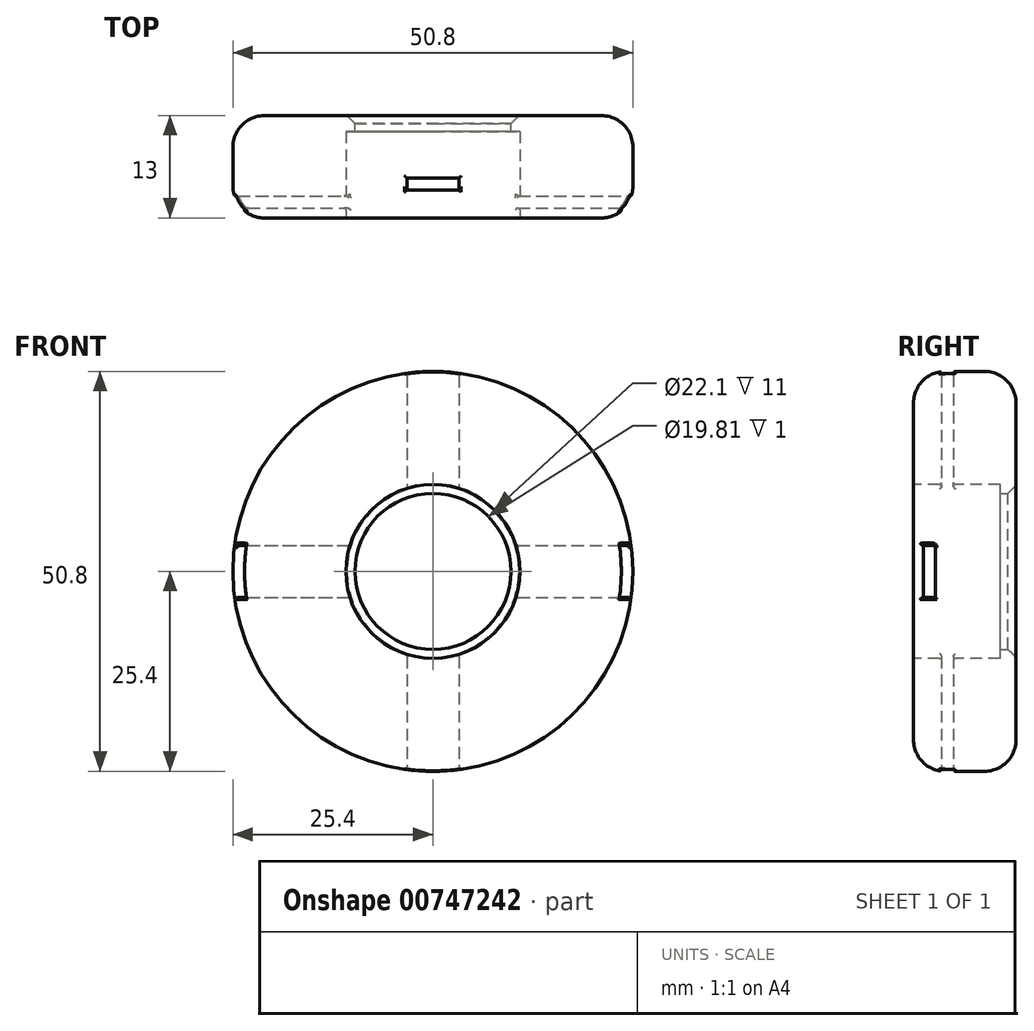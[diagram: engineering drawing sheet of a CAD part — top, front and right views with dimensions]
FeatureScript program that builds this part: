
annotation { "Feature Type Name" : "Feature", "Feature Type Description" : "" }
export const myFeature = defineFeature(function(context is Context, id is Id, definition is map)
    precondition{}
    {
        {
            var Q0;
            Q0=qCreatedBy(makeId("Front.planeOp"),FACE);
            var sketch = newSketch(context, id + "F0", { "sketchPlane" : qUnion([Q0])});
            skCircle(sketch, "E0", {"center": v(0, 0) * mm, "radius": 25.4 * mm});
            skSolve(sketch);
        }
        {
            var Q0;
            Q0=makeQuery(id+"F0.imprint","IMPRINT",FACE,{"disambiguationData":[TD([[makeQuery(id+"F0.imprint","IMPRINT",EDGE,{"derivedFrom":sQuery(id+"F0.wireOp",EDGE,"E0")}),1.0]])]});
            extrude(context, id + "F1", {"entities" : qUnion([Q0]), "depth" : 13 * mm, "offsetDistance" : 25.4 * mm});
        }
        {
            var Q0;
            Q0=qCreatedBy(makeId("Right.planeOp"),FACE);
            var sketch = newSketch(context, id + "F2", { "sketchPlane" : qUnion([Q0])});
            skLineSegment(sketch, "E1.bottom", {"start": v(-11.73, -3.3) * mm, "end": v(-10.2, -3.3) * mm});
            skLineSegment(sketch, "E1.top", {"start": v(-11.73, 3.3) * mm, "end": v(-10.2, 3.3) * mm});
            skLineSegment(sketch, "E1.left", {"start": v(-11.73, -3.3) * mm, "end": v(-11.73, 3.3) * mm});
            skLineSegment(sketch, "E1.right", {"start": v(-10.2, -3.3) * mm, "end": v(-10.2, 3.3) * mm});
            skSolve(sketch);
        }
        {
            var Q0;
            Q0 = qSketchRegion(id + "F2", true);
            extrude(context, id + "F3", {"entities" : qUnion([Q0]), "operationType" : NewBodyOperationType.REMOVE, "endBound" : BoundingType.THROUGH_ALL, "oppositeDirection" : true, "depth" : 25.4 * mm, "offsetDistance" : 25.4 * mm, "hasSecondDirection" : true, "secondDirectionOppositeDirection" : false, "secondDirectionDepth" : 25.4 * mm});
        }
        {
            var Q0;
            Q0=qCreatedBy(makeId("Top.planeOp"),FACE);
            var sketch = newSketch(context, id + "F4", { "sketchPlane" : qUnion([Q0])});
            skLineSegment(sketch, "E2.bottom", {"start": v(-3.3, -9.44) * mm, "end": v(3.3, -9.44) * mm});
            skLineSegment(sketch, "E2.top", {"start": v(-3.3, -7.92) * mm, "end": v(3.3, -7.92) * mm});
            skLineSegment(sketch, "E2.left", {"start": v(-3.3, -9.44) * mm, "end": v(-3.3, -7.92) * mm});
            skLineSegment(sketch, "E2.right", {"start": v(3.3, -9.44) * mm, "end": v(3.3, -7.92) * mm});
            skSolve(sketch);
        }
        {
            var Q0;
            Q0 = qSketchRegion(id + "F4", true);
            extrude(context, id + "F5", {"entities" : qUnion([Q0]), "operationType" : NewBodyOperationType.REMOVE, "endBound" : BoundingType.THROUGH_ALL, "depth" : 25.4 * mm, "offsetDistance" : 25.4 * mm, "hasSecondDirection" : true, "secondDirectionOppositeDirection" : true, "secondDirectionDepth" : 25.4 * mm});
        }
        {
            var Q0;
            Q0=makeQuery(id+"F1.opExtrude","CAP_FACE",FACE,{"disambiguationData":[OSD([sQuery(id+"F0.wireOp",EDGE,"E0")])],"isStart":false});
            var sketch = newSketch(context, id + "F6", { "sketchPlane" : qUnion([Q0])});
            skCircle(sketch, "E3", {"center": v(0, 0) * mm, "radius": 11.05 * mm});
            skSolve(sketch);
        }
        {
            var Q0;
            Q0=makeQuery(id+"F6.imprint","IMPRINT",FACE,{"disambiguationData":[TD([[makeQuery(id+"F6.imprint","IMPRINT",EDGE,{"derivedFrom":sQuery(id+"F6.wireOp",EDGE,"hlIgMGkD-AqOv-XqT3-OBZ0-IdH9VKwmBdzJ")}),1.0]])]});
            var Q1;
            Q1=makeQuery(id+"F6.imprint","IMPRINT",FACE,{"disambiguationData":[TD([[makeQuery(id+"F6.imprint","IMPRINT",EDGE,{"derivedFrom":sQuery(id+"F6.wireOp",EDGE,"E3")}),1.0]])]});
            extrude(context, id + "F7", {"entities" : qUnion([Q0, Q1]), "operationType" : NewBodyOperationType.REMOVE, "endBound" : BoundingType.THROUGH_ALL, "oppositeDirection" : true, "depth" : 25.4 * mm, "offsetDistance" : 25.4 * mm});
        }
        {
            var Q0;
            Q0=qCreatedBy(makeId("Front.planeOp"),FACE);
            var sketch = newSketch(context, id + "F8", { "sketchPlane" : qUnion([Q0])});
            skCircle(sketch, "E4", {"center": v(0, 0) * mm, "radius": 9.9 * mm});
            skCircle(sketch, "E5", {"center": v(0, 0) * mm, "radius": 11.05 * mm});
            skSolve(sketch);
        }
        {
            var Q0;
            Q0=makeQuery(id+"F8.imprint","IMPRINT",FACE,{"disambiguationData":[TD([[makeQuery(id+"F8.imprint","IMPRINT",EDGE,{"derivedFrom":sQuery(id+"F8.wireOp",EDGE,"E4")}),-1.0]])]});
            extrude(context, id + "F9", {"entities" : qUnion([Q0]), "operationType" : NewBodyOperationType.ADD, "depth" : 2 * mm, "offsetDistance" : 25.4 * mm});
        }
        {
            var Q0;
            Q0=makeQuery(id+"F1.opExtrude","CAP_EDGE",EDGE,{"disambiguationData":[OSD([sQuery(id+"F0.wireOp",EDGE,"E0")])],"isStart":false});
            var Q1;
            Q1=makeQuery(id+"F1.opExtrude","CAP_EDGE",EDGE,{"disambiguationData":[OSD([sQuery(id+"F0.wireOp",EDGE,"E0")])],"isStart":true});
            fillet(context, id + "F10", {"entities" : qUnion([Q0, Q1]), "radius" : 4 * mm, "tangentPropagation" : true, "allowEdgeOverflow" : false});
        }
        {
            var Q0;
            Q0=makeQuery(id+"F7.boolean.opBoolean","COPY",EDGE,{"derivedFrom":makeQuery(id+"F7.opExtrude","CAP_EDGE",EDGE,{"disambiguationData":[OSD([sQuery(id+"F6.wireOp",EDGE,"E3")])],"isStart":true})});
            var Q1;
            Q1=makeQuery(id+"F9.opExtrude","CAP_EDGE",EDGE,{"disambiguationData":[OSD([sQuery(id+"F8.wireOp",EDGE,"E4")])],"isStart":true});
            chamfer(context, id + "F11", {"entities" : qUnion([Q0, Q1]), "width" : 1 * mm, "tangentPropagation" : true});
        }
        {
            var Q0;
            Q0=makeQuery(id+"F7.boolean.opBoolean","INTERSECT",EDGE,{"disambiguationData":[OD(3.0)],"derivedFrom":[makeQuery(id+"F5.boolean.opBoolean","MERGE",FACE,{"derivedFrom":[makeQuery(id+"F3.boolean.opBoolean","COPY",FACE,{"derivedFrom":makeQuery(id+"F3.opExtrude","SWEPT_FACE",FACE,{"disambiguationData":[OSD([sQuery(id+"F2.wireOp",EDGE,"E1.right")])]})}),makeQuery(id+"F5.opExtrude","SWEPT_FACE",FACE,{"disambiguationData":[OSD([sQuery(id+"F4.wireOp",EDGE,"E2.top")])]})]}),makeQuery(id+"F7.opExtrude","SWEPT_FACE",FACE,{"disambiguationData":[OSD([sQuery(id+"F6.wireOp",EDGE,"E3")])]})]});
            var Q1;
            Q1=makeQuery(id+"F7.boolean.opBoolean","INTERSECT",EDGE,{"derivedFrom":[makeQuery(id+"F5.boolean.opBoolean","COPY",FACE,{"disambiguationData":[TD([makeQuery(id+"F3.boolean.opBoolean","COPY",FACE,{"derivedFrom":makeQuery(id+"F3.opExtrude","SWEPT_FACE",FACE,{"disambiguationData":[OSD([sQuery(id+"F2.wireOp",EDGE,"E1.top")])]})})])],"derivedFrom":makeQuery(id+"F5.opExtrude","SWEPT_FACE",FACE,{"disambiguationData":[OSD([sQuery(id+"F4.wireOp",EDGE,"E2.left")])]})}),makeQuery(id+"F7.opExtrude","SWEPT_FACE",FACE,{"disambiguationData":[OSD([sQuery(id+"F6.wireOp",EDGE,"E3")])]})]});
            var Q2;
            Q2=makeQuery(id+"F7.boolean.opBoolean","INTERSECT",EDGE,{"disambiguationData":[OD(3.0)],"derivedFrom":[makeQuery(id+"F5.boolean.opBoolean","MERGE",FACE,{"derivedFrom":[makeQuery(id+"F3.boolean.opBoolean","COPY",FACE,{"derivedFrom":makeQuery(id+"F3.opExtrude","SWEPT_FACE",FACE,{"disambiguationData":[OSD([sQuery(id+"F2.wireOp",EDGE,"E1.left")])]})}),makeQuery(id+"F5.opExtrude","SWEPT_FACE",FACE,{"disambiguationData":[OSD([sQuery(id+"F4.wireOp",EDGE,"E2.bottom")])]})]}),makeQuery(id+"F7.opExtrude","SWEPT_FACE",FACE,{"disambiguationData":[OSD([sQuery(id+"F6.wireOp",EDGE,"E3")])]})]});
            var Q3;
            Q3=makeQuery(id+"F7.boolean.opBoolean","INTERSECT",EDGE,{"derivedFrom":[makeQuery(id+"F5.boolean.opBoolean","COPY",FACE,{"disambiguationData":[TD([makeQuery(id+"F3.boolean.opBoolean","COPY",FACE,{"derivedFrom":makeQuery(id+"F3.opExtrude","SWEPT_FACE",FACE,{"disambiguationData":[OSD([sQuery(id+"F2.wireOp",EDGE,"E1.top")])]})})])],"derivedFrom":makeQuery(id+"F5.opExtrude","SWEPT_FACE",FACE,{"disambiguationData":[OSD([sQuery(id+"F4.wireOp",EDGE,"E2.right")])]})}),makeQuery(id+"F7.opExtrude","SWEPT_FACE",FACE,{"disambiguationData":[OSD([sQuery(id+"F6.wireOp",EDGE,"E3")])]})]});
            var Q4;
            Q4=makeQuery(id+"F7.boolean.opBoolean","INTERSECT",EDGE,{"derivedFrom":[makeQuery(id+"F5.boolean.opBoolean","SPLIT",FACE,{"disambiguationData":[TD([makeQuery(id+"F5.opExtrude","SWEPT_FACE",FACE,{"disambiguationData":[OSD([sQuery(id+"F4.wireOp",EDGE,"E2.left")])]})])],"derivedFrom":makeQuery(id+"F3.boolean.opBoolean","COPY",FACE,{"derivedFrom":makeQuery(id+"F3.opExtrude","SWEPT_FACE",FACE,{"disambiguationData":[OSD([sQuery(id+"F2.wireOp",EDGE,"E1.top")])]})})}),makeQuery(id+"F7.opExtrude","SWEPT_FACE",FACE,{"disambiguationData":[OSD([sQuery(id+"F6.wireOp",EDGE,"E3")])]})]});
            var Q5;
            Q5=makeQuery(id+"F7.boolean.opBoolean","INTERSECT",EDGE,{"disambiguationData":[OD(0.0)],"derivedFrom":[makeQuery(id+"F5.boolean.opBoolean","MERGE",FACE,{"derivedFrom":[makeQuery(id+"F3.boolean.opBoolean","COPY",FACE,{"derivedFrom":makeQuery(id+"F3.opExtrude","SWEPT_FACE",FACE,{"disambiguationData":[OSD([sQuery(id+"F2.wireOp",EDGE,"E1.right")])]})}),makeQuery(id+"F5.opExtrude","SWEPT_FACE",FACE,{"disambiguationData":[OSD([sQuery(id+"F4.wireOp",EDGE,"E2.top")])]})]}),makeQuery(id+"F7.opExtrude","SWEPT_FACE",FACE,{"disambiguationData":[OSD([sQuery(id+"F6.wireOp",EDGE,"E3")])]})]});
            var Q6;
            Q6=makeQuery(id+"F7.boolean.opBoolean","INTERSECT",EDGE,{"disambiguationData":[OD(0.0)],"derivedFrom":[makeQuery(id+"F5.boolean.opBoolean","MERGE",FACE,{"derivedFrom":[makeQuery(id+"F3.boolean.opBoolean","COPY",FACE,{"derivedFrom":makeQuery(id+"F3.opExtrude","SWEPT_FACE",FACE,{"disambiguationData":[OSD([sQuery(id+"F2.wireOp",EDGE,"E1.left")])]})}),makeQuery(id+"F5.opExtrude","SWEPT_FACE",FACE,{"disambiguationData":[OSD([sQuery(id+"F4.wireOp",EDGE,"E2.bottom")])]})]}),makeQuery(id+"F7.opExtrude","SWEPT_FACE",FACE,{"disambiguationData":[OSD([sQuery(id+"F6.wireOp",EDGE,"E3")])]})]});
            var Q7;
            Q7=makeQuery(id+"F7.boolean.opBoolean","INTERSECT",EDGE,{"derivedFrom":[makeQuery(id+"F5.boolean.opBoolean","SPLIT",FACE,{"disambiguationData":[TD([makeQuery(id+"F5.opExtrude","SWEPT_FACE",FACE,{"disambiguationData":[OSD([sQuery(id+"F4.wireOp",EDGE,"E2.left")])]})])],"derivedFrom":makeQuery(id+"F3.boolean.opBoolean","COPY",FACE,{"derivedFrom":makeQuery(id+"F3.opExtrude","SWEPT_FACE",FACE,{"disambiguationData":[OSD([sQuery(id+"F2.wireOp",EDGE,"E1.bottom")])]})})}),makeQuery(id+"F7.opExtrude","SWEPT_FACE",FACE,{"disambiguationData":[OSD([sQuery(id+"F6.wireOp",EDGE,"E3")])]})]});
            var Q8;
            Q8=makeQuery(id+"F7.boolean.opBoolean","INTERSECT",EDGE,{"derivedFrom":[makeQuery(id+"F5.boolean.opBoolean","COPY",FACE,{"disambiguationData":[TD([makeQuery(id+"F3.boolean.opBoolean","COPY",FACE,{"derivedFrom":makeQuery(id+"F3.opExtrude","SWEPT_FACE",FACE,{"disambiguationData":[OSD([sQuery(id+"F2.wireOp",EDGE,"E1.bottom")])]})})])],"derivedFrom":makeQuery(id+"F5.opExtrude","SWEPT_FACE",FACE,{"disambiguationData":[OSD([sQuery(id+"F4.wireOp",EDGE,"E2.right")])]})}),makeQuery(id+"F7.opExtrude","SWEPT_FACE",FACE,{"disambiguationData":[OSD([sQuery(id+"F6.wireOp",EDGE,"E3")])]})]});
            var Q9;
            Q9=makeQuery(id+"F7.boolean.opBoolean","INTERSECT",EDGE,{"disambiguationData":[OD(2.0)],"derivedFrom":[makeQuery(id+"F5.boolean.opBoolean","MERGE",FACE,{"derivedFrom":[makeQuery(id+"F3.boolean.opBoolean","COPY",FACE,{"derivedFrom":makeQuery(id+"F3.opExtrude","SWEPT_FACE",FACE,{"disambiguationData":[OSD([sQuery(id+"F2.wireOp",EDGE,"E1.right")])]})}),makeQuery(id+"F5.opExtrude","SWEPT_FACE",FACE,{"disambiguationData":[OSD([sQuery(id+"F4.wireOp",EDGE,"E2.top")])]})]}),makeQuery(id+"F7.opExtrude","SWEPT_FACE",FACE,{"disambiguationData":[OSD([sQuery(id+"F6.wireOp",EDGE,"E3")])]})]});
            var Q10;
            Q10=makeQuery(id+"F7.boolean.opBoolean","INTERSECT",EDGE,{"derivedFrom":[makeQuery(id+"F5.boolean.opBoolean","COPY",FACE,{"disambiguationData":[TD([makeQuery(id+"F3.boolean.opBoolean","COPY",FACE,{"derivedFrom":makeQuery(id+"F3.opExtrude","SWEPT_FACE",FACE,{"disambiguationData":[OSD([sQuery(id+"F2.wireOp",EDGE,"E1.bottom")])]})})])],"derivedFrom":makeQuery(id+"F5.opExtrude","SWEPT_FACE",FACE,{"disambiguationData":[OSD([sQuery(id+"F4.wireOp",EDGE,"E2.left")])]})}),makeQuery(id+"F7.opExtrude","SWEPT_FACE",FACE,{"disambiguationData":[OSD([sQuery(id+"F6.wireOp",EDGE,"E3")])]})]});
            var Q11;
            Q11=makeQuery(id+"F7.boolean.opBoolean","INTERSECT",EDGE,{"disambiguationData":[OD(2.0)],"derivedFrom":[makeQuery(id+"F5.boolean.opBoolean","MERGE",FACE,{"derivedFrom":[makeQuery(id+"F3.boolean.opBoolean","COPY",FACE,{"derivedFrom":makeQuery(id+"F3.opExtrude","SWEPT_FACE",FACE,{"disambiguationData":[OSD([sQuery(id+"F2.wireOp",EDGE,"E1.left")])]})}),makeQuery(id+"F5.opExtrude","SWEPT_FACE",FACE,{"disambiguationData":[OSD([sQuery(id+"F4.wireOp",EDGE,"E2.bottom")])]})]}),makeQuery(id+"F7.opExtrude","SWEPT_FACE",FACE,{"disambiguationData":[OSD([sQuery(id+"F6.wireOp",EDGE,"E3")])]})]});
            var Q12;
            Q12=makeQuery(id+"F7.boolean.opBoolean","INTERSECT",EDGE,{"disambiguationData":[OD(1.0)],"derivedFrom":[makeQuery(id+"F5.boolean.opBoolean","MERGE",FACE,{"derivedFrom":[makeQuery(id+"F3.boolean.opBoolean","COPY",FACE,{"derivedFrom":makeQuery(id+"F3.opExtrude","SWEPT_FACE",FACE,{"disambiguationData":[OSD([sQuery(id+"F2.wireOp",EDGE,"E1.left")])]})}),makeQuery(id+"F5.opExtrude","SWEPT_FACE",FACE,{"disambiguationData":[OSD([sQuery(id+"F4.wireOp",EDGE,"E2.bottom")])]})]}),makeQuery(id+"F7.opExtrude","SWEPT_FACE",FACE,{"disambiguationData":[OSD([sQuery(id+"F6.wireOp",EDGE,"E3")])]})]});
            var Q13;
            Q13=makeQuery(id+"F7.boolean.opBoolean","INTERSECT",EDGE,{"disambiguationData":[OD(1.0)],"derivedFrom":[makeQuery(id+"F5.boolean.opBoolean","MERGE",FACE,{"derivedFrom":[makeQuery(id+"F3.boolean.opBoolean","COPY",FACE,{"derivedFrom":makeQuery(id+"F3.opExtrude","SWEPT_FACE",FACE,{"disambiguationData":[OSD([sQuery(id+"F2.wireOp",EDGE,"E1.right")])]})}),makeQuery(id+"F5.opExtrude","SWEPT_FACE",FACE,{"disambiguationData":[OSD([sQuery(id+"F4.wireOp",EDGE,"E2.top")])]})]}),makeQuery(id+"F7.opExtrude","SWEPT_FACE",FACE,{"disambiguationData":[OSD([sQuery(id+"F6.wireOp",EDGE,"E3")])]})]});
            var Q14;
            Q14=makeQuery(id+"F7.boolean.opBoolean","INTERSECT",EDGE,{"derivedFrom":[makeQuery(id+"F5.boolean.opBoolean","SPLIT",FACE,{"disambiguationData":[TD([makeQuery(id+"F5.opExtrude","SWEPT_FACE",FACE,{"disambiguationData":[OSD([sQuery(id+"F4.wireOp",EDGE,"E2.right")])]})])],"derivedFrom":makeQuery(id+"F3.boolean.opBoolean","COPY",FACE,{"derivedFrom":makeQuery(id+"F3.opExtrude","SWEPT_FACE",FACE,{"disambiguationData":[OSD([sQuery(id+"F2.wireOp",EDGE,"E1.bottom")])]})})}),makeQuery(id+"F7.opExtrude","SWEPT_FACE",FACE,{"disambiguationData":[OSD([sQuery(id+"F6.wireOp",EDGE,"E3")])]})]});
            var Q15;
            Q15=makeQuery(id+"F7.boolean.opBoolean","INTERSECT",EDGE,{"derivedFrom":[makeQuery(id+"F5.boolean.opBoolean","SPLIT",FACE,{"disambiguationData":[TD([makeQuery(id+"F5.opExtrude","SWEPT_FACE",FACE,{"disambiguationData":[OSD([sQuery(id+"F4.wireOp",EDGE,"E2.right")])]})])],"derivedFrom":makeQuery(id+"F3.boolean.opBoolean","COPY",FACE,{"derivedFrom":makeQuery(id+"F3.opExtrude","SWEPT_FACE",FACE,{"disambiguationData":[OSD([sQuery(id+"F2.wireOp",EDGE,"E1.top")])]})})}),makeQuery(id+"F7.opExtrude","SWEPT_FACE",FACE,{"disambiguationData":[OSD([sQuery(id+"F6.wireOp",EDGE,"E3")])]})]});
            var Q16;
            {var subQ0=sQuery(id+"F0.wireOp",EDGE,"E0");var subQ1=makeQuery(id+"F1.opExtrude","SWEPT_FACE",FACE,{"disambiguationData":[OSD([subQ0])]});var subQ2=makeQuery(id+"F3.boolean.opBoolean","COPY",FACE,{"derivedFrom":makeQuery(id+"F3.opExtrude","SWEPT_FACE",FACE,{"disambiguationData":[OSD([sQuery(id+"F2.wireOp",EDGE,"E1.right")])]})});var subQ4=makeQuery(id+"F3.boolean.opBoolean","COPY",FACE,{"derivedFrom":makeQuery(id+"F3.opExtrude","SWEPT_FACE",FACE,{"disambiguationData":[OSD([sQuery(id+"F2.wireOp",EDGE,"E1.top")])]})});var subQ6=makeQuery(id+"F5.opExtrude","SWEPT_FACE",FACE,{"disambiguationData":[OSD([sQuery(id+"F4.wireOp",EDGE,"E2.top")])]});Q16=makeQuery(id+"F10.opFillet","BLEND_EDGE",EDGE,{"blendedFrom":[makeQuery(id+"F1.opExtrude","CAP_EDGE",EDGE,{"disambiguationData":[OSD([subQ0])],"isStart":false}),makeQuery(id+"F7.boolean.opBoolean","SPLIT",FACE,{"disambiguationData":[TD([subQ1,makeQuery(id+"F5.boolean.opBoolean","COPY",FACE,{"disambiguationData":[TD([subQ4])],"derivedFrom":makeQuery(id+"F5.opExtrude","SWEPT_FACE",FACE,{"disambiguationData":[OSD([sQuery(id+"F4.wireOp",EDGE,"E2.left")])]})}),makeQuery(id+"F5.boolean.opBoolean","COPY",FACE,{"disambiguationData":[TD([subQ4])],"derivedFrom":makeQuery(id+"F5.opExtrude","SWEPT_FACE",FACE,{"disambiguationData":[OSD([sQuery(id+"F4.wireOp",EDGE,"E2.right")])]})}),makeQuery(id+"F7.opExtrude","SWEPT_FACE",FACE,{"disambiguationData":[OSD([sQuery(id+"F6.wireOp",EDGE,"E3")])]})])],"derivedFrom":makeQuery(id+"F5.boolean.opBoolean","MERGE",FACE,{"derivedFrom":[subQ2,subQ6]})})],"blendedInto":[makeQuery(id+"F7.boolean.opBoolean","SPLIT",FACE,{"disambiguationData":[TD([subQ1,makeQuery(id+"F5.boolean.opBoolean","COPY",FACE,{"disambiguationData":[TD([subQ4])],"derivedFrom":makeQuery(id+"F5.opExtrude","SWEPT_FACE",FACE,{"disambiguationData":[OSD([sQuery(id+"F4.wireOp",EDGE,"E2.left")])]})}),makeQuery(id+"F5.boolean.opBoolean","COPY",FACE,{"disambiguationData":[TD([subQ4])],"derivedFrom":makeQuery(id+"F5.opExtrude","SWEPT_FACE",FACE,{"disambiguationData":[OSD([sQuery(id+"F4.wireOp",EDGE,"E2.right")])]})}),makeQuery(id+"F7.opExtrude","SWEPT_FACE",FACE,{"disambiguationData":[OSD([sQuery(id+"F6.wireOp",EDGE,"E3")])]})])],"derivedFrom":makeQuery(id+"F5.boolean.opBoolean","MERGE",FACE,{"derivedFrom":[subQ2,subQ6]})})]});}
            var Q17;
            {var subQ0=sQuery(id+"F0.wireOp",EDGE,"E0");Q17=makeQuery(id+"F10.opFillet","BLEND_EDGE",EDGE,{"blendedFrom":[makeQuery(id+"F1.opExtrude","CAP_EDGE",EDGE,{"disambiguationData":[OSD([subQ0])],"isStart":false}),makeQuery(id+"F5.boolean.opBoolean","COPY",FACE,{"disambiguationData":[TD([makeQuery(id+"F3.boolean.opBoolean","COPY",FACE,{"derivedFrom":makeQuery(id+"F3.opExtrude","SWEPT_FACE",FACE,{"disambiguationData":[OSD([sQuery(id+"F2.wireOp",EDGE,"E1.top")])]})})])],"derivedFrom":makeQuery(id+"F5.opExtrude","SWEPT_FACE",FACE,{"disambiguationData":[OSD([sQuery(id+"F4.wireOp",EDGE,"E2.right")])]})})],"blendedInto":[makeQuery(id+"F5.boolean.opBoolean","COPY",FACE,{"disambiguationData":[TD([makeQuery(id+"F3.boolean.opBoolean","COPY",FACE,{"derivedFrom":makeQuery(id+"F3.opExtrude","SWEPT_FACE",FACE,{"disambiguationData":[OSD([sQuery(id+"F2.wireOp",EDGE,"E1.top")])]})})])],"derivedFrom":makeQuery(id+"F5.opExtrude","SWEPT_FACE",FACE,{"disambiguationData":[OSD([sQuery(id+"F4.wireOp",EDGE,"E2.right")])]})})]});}
            var Q18;
            {var subQ0=sQuery(id+"F0.wireOp",EDGE,"E0");var subQ1=makeQuery(id+"F1.opExtrude","SWEPT_FACE",FACE,{"disambiguationData":[OSD([subQ0])]});var subQ3=makeQuery(id+"F3.boolean.opBoolean","COPY",FACE,{"derivedFrom":makeQuery(id+"F3.opExtrude","SWEPT_FACE",FACE,{"disambiguationData":[OSD([sQuery(id+"F2.wireOp",EDGE,"E1.left")])]})});var subQ4=makeQuery(id+"F3.boolean.opBoolean","COPY",FACE,{"derivedFrom":makeQuery(id+"F3.opExtrude","SWEPT_FACE",FACE,{"disambiguationData":[OSD([sQuery(id+"F2.wireOp",EDGE,"E1.top")])]})});var subQ5=makeQuery(id+"F5.opExtrude","SWEPT_FACE",FACE,{"disambiguationData":[OSD([sQuery(id+"F4.wireOp",EDGE,"E2.bottom")])]});Q18=makeQuery(id+"F10.opFillet","BLEND_EDGE",EDGE,{"blendedFrom":[makeQuery(id+"F1.opExtrude","CAP_EDGE",EDGE,{"disambiguationData":[OSD([subQ0])],"isStart":false}),makeQuery(id+"F7.boolean.opBoolean","SPLIT",FACE,{"disambiguationData":[TD([subQ1,makeQuery(id+"F5.boolean.opBoolean","COPY",FACE,{"disambiguationData":[TD([subQ4])],"derivedFrom":makeQuery(id+"F5.opExtrude","SWEPT_FACE",FACE,{"disambiguationData":[OSD([sQuery(id+"F4.wireOp",EDGE,"E2.left")])]})}),makeQuery(id+"F5.boolean.opBoolean","COPY",FACE,{"disambiguationData":[TD([subQ4])],"derivedFrom":makeQuery(id+"F5.opExtrude","SWEPT_FACE",FACE,{"disambiguationData":[OSD([sQuery(id+"F4.wireOp",EDGE,"E2.right")])]})}),makeQuery(id+"F7.opExtrude","SWEPT_FACE",FACE,{"disambiguationData":[OSD([sQuery(id+"F6.wireOp",EDGE,"E3")])]})])],"derivedFrom":makeQuery(id+"F5.boolean.opBoolean","MERGE",FACE,{"derivedFrom":[subQ3,subQ5]})})],"blendedInto":[makeQuery(id+"F7.boolean.opBoolean","SPLIT",FACE,{"disambiguationData":[TD([subQ1,makeQuery(id+"F5.boolean.opBoolean","COPY",FACE,{"disambiguationData":[TD([subQ4])],"derivedFrom":makeQuery(id+"F5.opExtrude","SWEPT_FACE",FACE,{"disambiguationData":[OSD([sQuery(id+"F4.wireOp",EDGE,"E2.left")])]})}),makeQuery(id+"F5.boolean.opBoolean","COPY",FACE,{"disambiguationData":[TD([subQ4])],"derivedFrom":makeQuery(id+"F5.opExtrude","SWEPT_FACE",FACE,{"disambiguationData":[OSD([sQuery(id+"F4.wireOp",EDGE,"E2.right")])]})}),makeQuery(id+"F7.opExtrude","SWEPT_FACE",FACE,{"disambiguationData":[OSD([sQuery(id+"F6.wireOp",EDGE,"E3")])]})])],"derivedFrom":makeQuery(id+"F5.boolean.opBoolean","MERGE",FACE,{"derivedFrom":[subQ3,subQ5]})})]});}
            var Q19;
            {var subQ0=sQuery(id+"F0.wireOp",EDGE,"E0");Q19=makeQuery(id+"F10.opFillet","BLEND_EDGE",EDGE,{"blendedFrom":[makeQuery(id+"F1.opExtrude","CAP_EDGE",EDGE,{"disambiguationData":[OSD([subQ0])],"isStart":false}),makeQuery(id+"F5.boolean.opBoolean","COPY",FACE,{"disambiguationData":[TD([makeQuery(id+"F3.boolean.opBoolean","COPY",FACE,{"derivedFrom":makeQuery(id+"F3.opExtrude","SWEPT_FACE",FACE,{"disambiguationData":[OSD([sQuery(id+"F2.wireOp",EDGE,"E1.top")])]})})])],"derivedFrom":makeQuery(id+"F5.opExtrude","SWEPT_FACE",FACE,{"disambiguationData":[OSD([sQuery(id+"F4.wireOp",EDGE,"E2.left")])]})})],"blendedInto":[makeQuery(id+"F5.boolean.opBoolean","COPY",FACE,{"disambiguationData":[TD([makeQuery(id+"F3.boolean.opBoolean","COPY",FACE,{"derivedFrom":makeQuery(id+"F3.opExtrude","SWEPT_FACE",FACE,{"disambiguationData":[OSD([sQuery(id+"F2.wireOp",EDGE,"E1.top")])]})})])],"derivedFrom":makeQuery(id+"F5.opExtrude","SWEPT_FACE",FACE,{"disambiguationData":[OSD([sQuery(id+"F4.wireOp",EDGE,"E2.left")])]})})]});}
            var Q20;
            {var subQ0=sQuery(id+"F0.wireOp",EDGE,"E0");Q20=makeQuery(id+"F10.opFillet","BLEND_EDGE",EDGE,{"blendedFrom":[makeQuery(id+"F1.opExtrude","CAP_EDGE",EDGE,{"disambiguationData":[OSD([subQ0])],"isStart":false}),makeQuery(id+"F5.boolean.opBoolean","SPLIT",FACE,{"disambiguationData":[TD([makeQuery(id+"F5.opExtrude","SWEPT_FACE",FACE,{"disambiguationData":[OSD([sQuery(id+"F4.wireOp",EDGE,"E2.left")])]})])],"derivedFrom":makeQuery(id+"F3.boolean.opBoolean","COPY",FACE,{"derivedFrom":makeQuery(id+"F3.opExtrude","SWEPT_FACE",FACE,{"disambiguationData":[OSD([sQuery(id+"F2.wireOp",EDGE,"E1.bottom")])]})})})],"blendedInto":[makeQuery(id+"F5.boolean.opBoolean","SPLIT",FACE,{"disambiguationData":[TD([makeQuery(id+"F5.opExtrude","SWEPT_FACE",FACE,{"disambiguationData":[OSD([sQuery(id+"F4.wireOp",EDGE,"E2.left")])]})])],"derivedFrom":makeQuery(id+"F3.boolean.opBoolean","COPY",FACE,{"derivedFrom":makeQuery(id+"F3.opExtrude","SWEPT_FACE",FACE,{"disambiguationData":[OSD([sQuery(id+"F2.wireOp",EDGE,"E1.bottom")])]})})})]});}
            var Q21;
            {var subQ0=sQuery(id+"F0.wireOp",EDGE,"E0");Q21=makeQuery(id+"F10.opFillet","BLEND_EDGE",EDGE,{"blendedFrom":[makeQuery(id+"F1.opExtrude","CAP_EDGE",EDGE,{"disambiguationData":[OSD([subQ0])],"isStart":false}),makeQuery(id+"F7.boolean.opBoolean","SPLIT",FACE,{"disambiguationData":[TD([makeQuery(id+"F1.opExtrude","SWEPT_FACE",FACE,{"disambiguationData":[OSD([subQ0])]}),makeQuery(id+"F3.boolean.opBoolean","COPY",FACE,{"derivedFrom":makeQuery(id+"F3.opExtrude","SWEPT_FACE",FACE,{"disambiguationData":[OSD([sQuery(id+"F2.wireOp",EDGE,"E1.bottom")])]})}),makeQuery(id+"F3.boolean.opBoolean","COPY",FACE,{"derivedFrom":makeQuery(id+"F3.opExtrude","SWEPT_FACE",FACE,{"disambiguationData":[OSD([sQuery(id+"F2.wireOp",EDGE,"E1.top")])]})}),makeQuery(id+"F7.opExtrude","SWEPT_FACE",FACE,{"disambiguationData":[OSD([sQuery(id+"F6.wireOp",EDGE,"E3")])]})]),OD(0.0)],"derivedFrom":makeQuery(id+"F5.boolean.opBoolean","MERGE",FACE,{"derivedFrom":[makeQuery(id+"F3.boolean.opBoolean","COPY",FACE,{"derivedFrom":makeQuery(id+"F3.opExtrude","SWEPT_FACE",FACE,{"disambiguationData":[OSD([sQuery(id+"F2.wireOp",EDGE,"E1.right")])]})}),makeQuery(id+"F5.opExtrude","SWEPT_FACE",FACE,{"disambiguationData":[OSD([sQuery(id+"F4.wireOp",EDGE,"E2.top")])]})]})})],"blendedInto":[makeQuery(id+"F7.boolean.opBoolean","SPLIT",FACE,{"disambiguationData":[TD([makeQuery(id+"F1.opExtrude","SWEPT_FACE",FACE,{"disambiguationData":[OSD([subQ0])]}),makeQuery(id+"F3.boolean.opBoolean","COPY",FACE,{"derivedFrom":makeQuery(id+"F3.opExtrude","SWEPT_FACE",FACE,{"disambiguationData":[OSD([sQuery(id+"F2.wireOp",EDGE,"E1.bottom")])]})}),makeQuery(id+"F3.boolean.opBoolean","COPY",FACE,{"derivedFrom":makeQuery(id+"F3.opExtrude","SWEPT_FACE",FACE,{"disambiguationData":[OSD([sQuery(id+"F2.wireOp",EDGE,"E1.top")])]})}),makeQuery(id+"F7.opExtrude","SWEPT_FACE",FACE,{"disambiguationData":[OSD([sQuery(id+"F6.wireOp",EDGE,"E3")])]})]),OD(0.0)],"derivedFrom":makeQuery(id+"F5.boolean.opBoolean","MERGE",FACE,{"derivedFrom":[makeQuery(id+"F3.boolean.opBoolean","COPY",FACE,{"derivedFrom":makeQuery(id+"F3.opExtrude","SWEPT_FACE",FACE,{"disambiguationData":[OSD([sQuery(id+"F2.wireOp",EDGE,"E1.right")])]})}),makeQuery(id+"F5.opExtrude","SWEPT_FACE",FACE,{"disambiguationData":[OSD([sQuery(id+"F4.wireOp",EDGE,"E2.top")])]})]})})]});}
            var Q22;
            {var subQ0=sQuery(id+"F0.wireOp",EDGE,"E0");Q22=makeQuery(id+"F10.opFillet","BLEND_EDGE",EDGE,{"blendedFrom":[makeQuery(id+"F1.opExtrude","CAP_EDGE",EDGE,{"disambiguationData":[OSD([subQ0])],"isStart":false}),makeQuery(id+"F7.boolean.opBoolean","SPLIT",FACE,{"disambiguationData":[TD([makeQuery(id+"F1.opExtrude","SWEPT_FACE",FACE,{"disambiguationData":[OSD([subQ0])]}),makeQuery(id+"F3.boolean.opBoolean","COPY",FACE,{"derivedFrom":makeQuery(id+"F3.opExtrude","SWEPT_FACE",FACE,{"disambiguationData":[OSD([sQuery(id+"F2.wireOp",EDGE,"E1.bottom")])]})}),makeQuery(id+"F3.boolean.opBoolean","COPY",FACE,{"derivedFrom":makeQuery(id+"F3.opExtrude","SWEPT_FACE",FACE,{"disambiguationData":[OSD([sQuery(id+"F2.wireOp",EDGE,"E1.top")])]})}),makeQuery(id+"F7.opExtrude","SWEPT_FACE",FACE,{"disambiguationData":[OSD([sQuery(id+"F6.wireOp",EDGE,"E3")])]})]),OD(0.0)],"derivedFrom":makeQuery(id+"F5.boolean.opBoolean","MERGE",FACE,{"derivedFrom":[makeQuery(id+"F3.boolean.opBoolean","COPY",FACE,{"derivedFrom":makeQuery(id+"F3.opExtrude","SWEPT_FACE",FACE,{"disambiguationData":[OSD([sQuery(id+"F2.wireOp",EDGE,"E1.left")])]})}),makeQuery(id+"F5.opExtrude","SWEPT_FACE",FACE,{"disambiguationData":[OSD([sQuery(id+"F4.wireOp",EDGE,"E2.bottom")])]})]})})],"blendedInto":[makeQuery(id+"F7.boolean.opBoolean","SPLIT",FACE,{"disambiguationData":[TD([makeQuery(id+"F1.opExtrude","SWEPT_FACE",FACE,{"disambiguationData":[OSD([subQ0])]}),makeQuery(id+"F3.boolean.opBoolean","COPY",FACE,{"derivedFrom":makeQuery(id+"F3.opExtrude","SWEPT_FACE",FACE,{"disambiguationData":[OSD([sQuery(id+"F2.wireOp",EDGE,"E1.bottom")])]})}),makeQuery(id+"F3.boolean.opBoolean","COPY",FACE,{"derivedFrom":makeQuery(id+"F3.opExtrude","SWEPT_FACE",FACE,{"disambiguationData":[OSD([sQuery(id+"F2.wireOp",EDGE,"E1.top")])]})}),makeQuery(id+"F7.opExtrude","SWEPT_FACE",FACE,{"disambiguationData":[OSD([sQuery(id+"F6.wireOp",EDGE,"E3")])]})]),OD(0.0)],"derivedFrom":makeQuery(id+"F5.boolean.opBoolean","MERGE",FACE,{"derivedFrom":[makeQuery(id+"F3.boolean.opBoolean","COPY",FACE,{"derivedFrom":makeQuery(id+"F3.opExtrude","SWEPT_FACE",FACE,{"disambiguationData":[OSD([sQuery(id+"F2.wireOp",EDGE,"E1.left")])]})}),makeQuery(id+"F5.opExtrude","SWEPT_FACE",FACE,{"disambiguationData":[OSD([sQuery(id+"F4.wireOp",EDGE,"E2.bottom")])]})]})})]});}
            var Q23;
            {var subQ0=sQuery(id+"F2.wireOp",EDGE,"E1.right");var subQ1=sQuery(id+"F2.wireOp",EDGE,"E1.top");Q23=makeQuery(id+"F5.boolean.opBoolean","SPLIT",EDGE,{"disambiguationData":[TD([makeQuery(id+"F5.opExtrude","SWEPT_FACE",FACE,{"disambiguationData":[OSD([sQuery(id+"F4.wireOp",EDGE,"E2.left")])]})])],"derivedFrom":makeQuery(id+"F3.boolean.opBoolean","COPY",EDGE,{"derivedFrom":makeQuery(id+"F3.opExtrude","SWEPT_EDGE",EDGE,{"disambiguationData":[OSD([subQ1,subQ0])]})})});}
            var Q24;
            {var subQ0=sQuery(id+"F0.wireOp",EDGE,"E0");Q24=makeQuery(id+"F10.opFillet","BLEND_EDGE",EDGE,{"blendedFrom":[makeQuery(id+"F1.opExtrude","CAP_EDGE",EDGE,{"disambiguationData":[OSD([subQ0])],"isStart":false}),makeQuery(id+"F5.boolean.opBoolean","COPY",FACE,{"disambiguationData":[TD([makeQuery(id+"F3.boolean.opBoolean","COPY",FACE,{"derivedFrom":makeQuery(id+"F3.opExtrude","SWEPT_FACE",FACE,{"disambiguationData":[OSD([sQuery(id+"F2.wireOp",EDGE,"E1.bottom")])]})})])],"derivedFrom":makeQuery(id+"F5.opExtrude","SWEPT_FACE",FACE,{"disambiguationData":[OSD([sQuery(id+"F4.wireOp",EDGE,"E2.right")])]})})],"blendedInto":[makeQuery(id+"F5.boolean.opBoolean","COPY",FACE,{"disambiguationData":[TD([makeQuery(id+"F3.boolean.opBoolean","COPY",FACE,{"derivedFrom":makeQuery(id+"F3.opExtrude","SWEPT_FACE",FACE,{"disambiguationData":[OSD([sQuery(id+"F2.wireOp",EDGE,"E1.bottom")])]})})])],"derivedFrom":makeQuery(id+"F5.opExtrude","SWEPT_FACE",FACE,{"disambiguationData":[OSD([sQuery(id+"F4.wireOp",EDGE,"E2.right")])]})})]});}
            var Q25;
            {var subQ0=sQuery(id+"F0.wireOp",EDGE,"E0");var subQ1=makeQuery(id+"F1.opExtrude","SWEPT_FACE",FACE,{"disambiguationData":[OSD([subQ0])]});var subQ3=makeQuery(id+"F3.boolean.opBoolean","COPY",FACE,{"derivedFrom":makeQuery(id+"F3.opExtrude","SWEPT_FACE",FACE,{"disambiguationData":[OSD([sQuery(id+"F2.wireOp",EDGE,"E1.left")])]})});var subQ4=makeQuery(id+"F3.boolean.opBoolean","COPY",FACE,{"derivedFrom":makeQuery(id+"F3.opExtrude","SWEPT_FACE",FACE,{"disambiguationData":[OSD([sQuery(id+"F2.wireOp",EDGE,"E1.bottom")])]})});var subQ5=makeQuery(id+"F5.opExtrude","SWEPT_FACE",FACE,{"disambiguationData":[OSD([sQuery(id+"F4.wireOp",EDGE,"E2.bottom")])]});Q25=makeQuery(id+"F10.opFillet","BLEND_EDGE",EDGE,{"blendedFrom":[makeQuery(id+"F1.opExtrude","CAP_EDGE",EDGE,{"disambiguationData":[OSD([subQ0])],"isStart":false}),makeQuery(id+"F7.boolean.opBoolean","SPLIT",FACE,{"disambiguationData":[TD([subQ1,makeQuery(id+"F5.boolean.opBoolean","COPY",FACE,{"disambiguationData":[TD([subQ4])],"derivedFrom":makeQuery(id+"F5.opExtrude","SWEPT_FACE",FACE,{"disambiguationData":[OSD([sQuery(id+"F4.wireOp",EDGE,"E2.left")])]})}),makeQuery(id+"F5.boolean.opBoolean","COPY",FACE,{"disambiguationData":[TD([subQ4])],"derivedFrom":makeQuery(id+"F5.opExtrude","SWEPT_FACE",FACE,{"disambiguationData":[OSD([sQuery(id+"F4.wireOp",EDGE,"E2.right")])]})}),makeQuery(id+"F7.opExtrude","SWEPT_FACE",FACE,{"disambiguationData":[OSD([sQuery(id+"F6.wireOp",EDGE,"E3")])]})])],"derivedFrom":makeQuery(id+"F5.boolean.opBoolean","MERGE",FACE,{"derivedFrom":[subQ3,subQ5]})})],"blendedInto":[makeQuery(id+"F7.boolean.opBoolean","SPLIT",FACE,{"disambiguationData":[TD([subQ1,makeQuery(id+"F5.boolean.opBoolean","COPY",FACE,{"disambiguationData":[TD([subQ4])],"derivedFrom":makeQuery(id+"F5.opExtrude","SWEPT_FACE",FACE,{"disambiguationData":[OSD([sQuery(id+"F4.wireOp",EDGE,"E2.left")])]})}),makeQuery(id+"F5.boolean.opBoolean","COPY",FACE,{"disambiguationData":[TD([subQ4])],"derivedFrom":makeQuery(id+"F5.opExtrude","SWEPT_FACE",FACE,{"disambiguationData":[OSD([sQuery(id+"F4.wireOp",EDGE,"E2.right")])]})}),makeQuery(id+"F7.opExtrude","SWEPT_FACE",FACE,{"disambiguationData":[OSD([sQuery(id+"F6.wireOp",EDGE,"E3")])]})])],"derivedFrom":makeQuery(id+"F5.boolean.opBoolean","MERGE",FACE,{"derivedFrom":[subQ3,subQ5]})})]});}
            var Q26;
            {var subQ0=sQuery(id+"F0.wireOp",EDGE,"E0");var subQ1=makeQuery(id+"F1.opExtrude","SWEPT_FACE",FACE,{"disambiguationData":[OSD([subQ0])]});var subQ2=makeQuery(id+"F3.boolean.opBoolean","COPY",FACE,{"derivedFrom":makeQuery(id+"F3.opExtrude","SWEPT_FACE",FACE,{"disambiguationData":[OSD([sQuery(id+"F2.wireOp",EDGE,"E1.right")])]})});var subQ4=makeQuery(id+"F3.boolean.opBoolean","COPY",FACE,{"derivedFrom":makeQuery(id+"F3.opExtrude","SWEPT_FACE",FACE,{"disambiguationData":[OSD([sQuery(id+"F2.wireOp",EDGE,"E1.bottom")])]})});var subQ6=makeQuery(id+"F5.opExtrude","SWEPT_FACE",FACE,{"disambiguationData":[OSD([sQuery(id+"F4.wireOp",EDGE,"E2.top")])]});Q26=makeQuery(id+"F10.opFillet","BLEND_EDGE",EDGE,{"blendedFrom":[makeQuery(id+"F1.opExtrude","CAP_EDGE",EDGE,{"disambiguationData":[OSD([subQ0])],"isStart":false}),makeQuery(id+"F7.boolean.opBoolean","SPLIT",FACE,{"disambiguationData":[TD([subQ1,makeQuery(id+"F5.boolean.opBoolean","COPY",FACE,{"disambiguationData":[TD([subQ4])],"derivedFrom":makeQuery(id+"F5.opExtrude","SWEPT_FACE",FACE,{"disambiguationData":[OSD([sQuery(id+"F4.wireOp",EDGE,"E2.left")])]})}),makeQuery(id+"F5.boolean.opBoolean","COPY",FACE,{"disambiguationData":[TD([subQ4])],"derivedFrom":makeQuery(id+"F5.opExtrude","SWEPT_FACE",FACE,{"disambiguationData":[OSD([sQuery(id+"F4.wireOp",EDGE,"E2.right")])]})}),makeQuery(id+"F7.opExtrude","SWEPT_FACE",FACE,{"disambiguationData":[OSD([sQuery(id+"F6.wireOp",EDGE,"E3")])]})])],"derivedFrom":makeQuery(id+"F5.boolean.opBoolean","MERGE",FACE,{"derivedFrom":[subQ2,subQ6]})})],"blendedInto":[makeQuery(id+"F7.boolean.opBoolean","SPLIT",FACE,{"disambiguationData":[TD([subQ1,makeQuery(id+"F5.boolean.opBoolean","COPY",FACE,{"disambiguationData":[TD([subQ4])],"derivedFrom":makeQuery(id+"F5.opExtrude","SWEPT_FACE",FACE,{"disambiguationData":[OSD([sQuery(id+"F4.wireOp",EDGE,"E2.left")])]})}),makeQuery(id+"F5.boolean.opBoolean","COPY",FACE,{"disambiguationData":[TD([subQ4])],"derivedFrom":makeQuery(id+"F5.opExtrude","SWEPT_FACE",FACE,{"disambiguationData":[OSD([sQuery(id+"F4.wireOp",EDGE,"E2.right")])]})}),makeQuery(id+"F7.opExtrude","SWEPT_FACE",FACE,{"disambiguationData":[OSD([sQuery(id+"F6.wireOp",EDGE,"E3")])]})])],"derivedFrom":makeQuery(id+"F5.boolean.opBoolean","MERGE",FACE,{"derivedFrom":[subQ2,subQ6]})})]});}
            var Q27;
            {var subQ0=sQuery(id+"F0.wireOp",EDGE,"E0");Q27=makeQuery(id+"F10.opFillet","BLEND_EDGE",EDGE,{"blendedFrom":[makeQuery(id+"F1.opExtrude","CAP_EDGE",EDGE,{"disambiguationData":[OSD([subQ0])],"isStart":false}),makeQuery(id+"F5.boolean.opBoolean","COPY",FACE,{"disambiguationData":[TD([makeQuery(id+"F3.boolean.opBoolean","COPY",FACE,{"derivedFrom":makeQuery(id+"F3.opExtrude","SWEPT_FACE",FACE,{"disambiguationData":[OSD([sQuery(id+"F2.wireOp",EDGE,"E1.bottom")])]})})])],"derivedFrom":makeQuery(id+"F5.opExtrude","SWEPT_FACE",FACE,{"disambiguationData":[OSD([sQuery(id+"F4.wireOp",EDGE,"E2.left")])]})})],"blendedInto":[makeQuery(id+"F5.boolean.opBoolean","COPY",FACE,{"disambiguationData":[TD([makeQuery(id+"F3.boolean.opBoolean","COPY",FACE,{"derivedFrom":makeQuery(id+"F3.opExtrude","SWEPT_FACE",FACE,{"disambiguationData":[OSD([sQuery(id+"F2.wireOp",EDGE,"E1.bottom")])]})})])],"derivedFrom":makeQuery(id+"F5.opExtrude","SWEPT_FACE",FACE,{"disambiguationData":[OSD([sQuery(id+"F4.wireOp",EDGE,"E2.left")])]})})]});}
            var Q28;
            {var subQ0=sQuery(id+"F0.wireOp",EDGE,"E0");Q28=makeQuery(id+"F10.opFillet","BLEND_EDGE",EDGE,{"blendedFrom":[makeQuery(id+"F1.opExtrude","CAP_EDGE",EDGE,{"disambiguationData":[OSD([subQ0])],"isStart":false}),makeQuery(id+"F7.boolean.opBoolean","SPLIT",FACE,{"disambiguationData":[TD([makeQuery(id+"F1.opExtrude","SWEPT_FACE",FACE,{"disambiguationData":[OSD([subQ0])]}),makeQuery(id+"F3.boolean.opBoolean","COPY",FACE,{"derivedFrom":makeQuery(id+"F3.opExtrude","SWEPT_FACE",FACE,{"disambiguationData":[OSD([sQuery(id+"F2.wireOp",EDGE,"E1.bottom")])]})}),makeQuery(id+"F3.boolean.opBoolean","COPY",FACE,{"derivedFrom":makeQuery(id+"F3.opExtrude","SWEPT_FACE",FACE,{"disambiguationData":[OSD([sQuery(id+"F2.wireOp",EDGE,"E1.top")])]})}),makeQuery(id+"F7.opExtrude","SWEPT_FACE",FACE,{"disambiguationData":[OSD([sQuery(id+"F6.wireOp",EDGE,"E3")])]})]),OD(1.0)],"derivedFrom":makeQuery(id+"F5.boolean.opBoolean","MERGE",FACE,{"derivedFrom":[makeQuery(id+"F3.boolean.opBoolean","COPY",FACE,{"derivedFrom":makeQuery(id+"F3.opExtrude","SWEPT_FACE",FACE,{"disambiguationData":[OSD([sQuery(id+"F2.wireOp",EDGE,"E1.right")])]})}),makeQuery(id+"F5.opExtrude","SWEPT_FACE",FACE,{"disambiguationData":[OSD([sQuery(id+"F4.wireOp",EDGE,"E2.top")])]})]})})],"blendedInto":[makeQuery(id+"F7.boolean.opBoolean","SPLIT",FACE,{"disambiguationData":[TD([makeQuery(id+"F1.opExtrude","SWEPT_FACE",FACE,{"disambiguationData":[OSD([subQ0])]}),makeQuery(id+"F3.boolean.opBoolean","COPY",FACE,{"derivedFrom":makeQuery(id+"F3.opExtrude","SWEPT_FACE",FACE,{"disambiguationData":[OSD([sQuery(id+"F2.wireOp",EDGE,"E1.bottom")])]})}),makeQuery(id+"F3.boolean.opBoolean","COPY",FACE,{"derivedFrom":makeQuery(id+"F3.opExtrude","SWEPT_FACE",FACE,{"disambiguationData":[OSD([sQuery(id+"F2.wireOp",EDGE,"E1.top")])]})}),makeQuery(id+"F7.opExtrude","SWEPT_FACE",FACE,{"disambiguationData":[OSD([sQuery(id+"F6.wireOp",EDGE,"E3")])]})]),OD(1.0)],"derivedFrom":makeQuery(id+"F5.boolean.opBoolean","MERGE",FACE,{"derivedFrom":[makeQuery(id+"F3.boolean.opBoolean","COPY",FACE,{"derivedFrom":makeQuery(id+"F3.opExtrude","SWEPT_FACE",FACE,{"disambiguationData":[OSD([sQuery(id+"F2.wireOp",EDGE,"E1.right")])]})}),makeQuery(id+"F5.opExtrude","SWEPT_FACE",FACE,{"disambiguationData":[OSD([sQuery(id+"F4.wireOp",EDGE,"E2.top")])]})]})})]});}
            var Q29;
            {var subQ0=sQuery(id+"F0.wireOp",EDGE,"E0");Q29=makeQuery(id+"F10.opFillet","BLEND_EDGE",EDGE,{"blendedFrom":[makeQuery(id+"F1.opExtrude","CAP_EDGE",EDGE,{"disambiguationData":[OSD([subQ0])],"isStart":false}),makeQuery(id+"F5.boolean.opBoolean","SPLIT",FACE,{"disambiguationData":[TD([makeQuery(id+"F5.opExtrude","SWEPT_FACE",FACE,{"disambiguationData":[OSD([sQuery(id+"F4.wireOp",EDGE,"E2.right")])]})])],"derivedFrom":makeQuery(id+"F3.boolean.opBoolean","COPY",FACE,{"derivedFrom":makeQuery(id+"F3.opExtrude","SWEPT_FACE",FACE,{"disambiguationData":[OSD([sQuery(id+"F2.wireOp",EDGE,"E1.top")])]})})})],"blendedInto":[makeQuery(id+"F5.boolean.opBoolean","SPLIT",FACE,{"disambiguationData":[TD([makeQuery(id+"F5.opExtrude","SWEPT_FACE",FACE,{"disambiguationData":[OSD([sQuery(id+"F4.wireOp",EDGE,"E2.right")])]})])],"derivedFrom":makeQuery(id+"F3.boolean.opBoolean","COPY",FACE,{"derivedFrom":makeQuery(id+"F3.opExtrude","SWEPT_FACE",FACE,{"disambiguationData":[OSD([sQuery(id+"F2.wireOp",EDGE,"E1.top")])]})})})]});}
            var Q30;
            {var subQ0=sQuery(id+"F0.wireOp",EDGE,"E0");Q30=makeQuery(id+"F10.opFillet","BLEND_EDGE",EDGE,{"blendedFrom":[makeQuery(id+"F1.opExtrude","CAP_EDGE",EDGE,{"disambiguationData":[OSD([subQ0])],"isStart":false}),makeQuery(id+"F7.boolean.opBoolean","SPLIT",FACE,{"disambiguationData":[TD([makeQuery(id+"F1.opExtrude","SWEPT_FACE",FACE,{"disambiguationData":[OSD([subQ0])]}),makeQuery(id+"F3.boolean.opBoolean","COPY",FACE,{"derivedFrom":makeQuery(id+"F3.opExtrude","SWEPT_FACE",FACE,{"disambiguationData":[OSD([sQuery(id+"F2.wireOp",EDGE,"E1.bottom")])]})}),makeQuery(id+"F3.boolean.opBoolean","COPY",FACE,{"derivedFrom":makeQuery(id+"F3.opExtrude","SWEPT_FACE",FACE,{"disambiguationData":[OSD([sQuery(id+"F2.wireOp",EDGE,"E1.top")])]})}),makeQuery(id+"F7.opExtrude","SWEPT_FACE",FACE,{"disambiguationData":[OSD([sQuery(id+"F6.wireOp",EDGE,"E3")])]})]),OD(1.0)],"derivedFrom":makeQuery(id+"F5.boolean.opBoolean","MERGE",FACE,{"derivedFrom":[makeQuery(id+"F3.boolean.opBoolean","COPY",FACE,{"derivedFrom":makeQuery(id+"F3.opExtrude","SWEPT_FACE",FACE,{"disambiguationData":[OSD([sQuery(id+"F2.wireOp",EDGE,"E1.left")])]})}),makeQuery(id+"F5.opExtrude","SWEPT_FACE",FACE,{"disambiguationData":[OSD([sQuery(id+"F4.wireOp",EDGE,"E2.bottom")])]})]})})],"blendedInto":[makeQuery(id+"F7.boolean.opBoolean","SPLIT",FACE,{"disambiguationData":[TD([makeQuery(id+"F1.opExtrude","SWEPT_FACE",FACE,{"disambiguationData":[OSD([subQ0])]}),makeQuery(id+"F3.boolean.opBoolean","COPY",FACE,{"derivedFrom":makeQuery(id+"F3.opExtrude","SWEPT_FACE",FACE,{"disambiguationData":[OSD([sQuery(id+"F2.wireOp",EDGE,"E1.bottom")])]})}),makeQuery(id+"F3.boolean.opBoolean","COPY",FACE,{"derivedFrom":makeQuery(id+"F3.opExtrude","SWEPT_FACE",FACE,{"disambiguationData":[OSD([sQuery(id+"F2.wireOp",EDGE,"E1.top")])]})}),makeQuery(id+"F7.opExtrude","SWEPT_FACE",FACE,{"disambiguationData":[OSD([sQuery(id+"F6.wireOp",EDGE,"E3")])]})]),OD(1.0)],"derivedFrom":makeQuery(id+"F5.boolean.opBoolean","MERGE",FACE,{"derivedFrom":[makeQuery(id+"F3.boolean.opBoolean","COPY",FACE,{"derivedFrom":makeQuery(id+"F3.opExtrude","SWEPT_FACE",FACE,{"disambiguationData":[OSD([sQuery(id+"F2.wireOp",EDGE,"E1.left")])]})}),makeQuery(id+"F5.opExtrude","SWEPT_FACE",FACE,{"disambiguationData":[OSD([sQuery(id+"F4.wireOp",EDGE,"E2.bottom")])]})]})})]});}
            var Q31;
            {var subQ0=sQuery(id+"F0.wireOp",EDGE,"E0");Q31=makeQuery(id+"F10.opFillet","BLEND_EDGE",EDGE,{"blendedFrom":[makeQuery(id+"F1.opExtrude","CAP_EDGE",EDGE,{"disambiguationData":[OSD([subQ0])],"isStart":false}),makeQuery(id+"F5.boolean.opBoolean","SPLIT",FACE,{"disambiguationData":[TD([makeQuery(id+"F5.opExtrude","SWEPT_FACE",FACE,{"disambiguationData":[OSD([sQuery(id+"F4.wireOp",EDGE,"E2.right")])]})])],"derivedFrom":makeQuery(id+"F3.boolean.opBoolean","COPY",FACE,{"derivedFrom":makeQuery(id+"F3.opExtrude","SWEPT_FACE",FACE,{"disambiguationData":[OSD([sQuery(id+"F2.wireOp",EDGE,"E1.bottom")])]})})})],"blendedInto":[makeQuery(id+"F5.boolean.opBoolean","SPLIT",FACE,{"disambiguationData":[TD([makeQuery(id+"F5.opExtrude","SWEPT_FACE",FACE,{"disambiguationData":[OSD([sQuery(id+"F4.wireOp",EDGE,"E2.right")])]})])],"derivedFrom":makeQuery(id+"F3.boolean.opBoolean","COPY",FACE,{"derivedFrom":makeQuery(id+"F3.opExtrude","SWEPT_FACE",FACE,{"disambiguationData":[OSD([sQuery(id+"F2.wireOp",EDGE,"E1.bottom")])]})})})]});}
            var Q32;
            Q32=makeQuery(id+"F10.opFillet","BLEND_EDGE",EDGE,{"blendedFrom":[makeQuery(id+"F1.opExtrude","CAP_EDGE",EDGE,{"disambiguationData":[OSD([sQuery(id+"F0.wireOp",EDGE,"E0")])],"isStart":false}),makeQuery(id+"F7.boolean.opBoolean","SPLIT",FACE,{"disambiguationData":[OD(0.0)],"derivedFrom":makeQuery(id+"F5.boolean.opBoolean","COPY",FACE,{"derivedFrom":makeQuery(id+"F5.opExtrude","SWEPT_FACE",FACE,{"disambiguationData":[OSD([sQuery(id+"F4.wireOp",EDGE,"E2.bottom")])]})})})],"blendedInto":[makeQuery(id+"F7.boolean.opBoolean","SPLIT",FACE,{"disambiguationData":[OD(0.0)],"derivedFrom":makeQuery(id+"F5.boolean.opBoolean","COPY",FACE,{"derivedFrom":makeQuery(id+"F5.opExtrude","SWEPT_FACE",FACE,{"disambiguationData":[OSD([sQuery(id+"F4.wireOp",EDGE,"E2.bottom")])]})})})]});
            var Q33;
            Q33=makeQuery(id+"F5.boolean.opBoolean","INTERSECT",EDGE,{"disambiguationData":[OD(0.0)],"derivedFrom":[makeQuery(id+"F1.opExtrude","SWEPT_FACE",FACE,{"disambiguationData":[OSD([sQuery(id+"F0.wireOp",EDGE,"E0")])]}),makeQuery(id+"F5.opExtrude","SWEPT_FACE",FACE,{"disambiguationData":[OSD([sQuery(id+"F4.wireOp",EDGE,"E2.top")])]})]});
            var Q34;
            Q34=makeQuery(id+"F7.boolean.opBoolean","INTERSECT",EDGE,{"disambiguationData":[OD(1.0)],"derivedFrom":[makeQuery(id+"F5.boolean.opBoolean","COPY",FACE,{"derivedFrom":makeQuery(id+"F5.opExtrude","SWEPT_FACE",FACE,{"disambiguationData":[OSD([sQuery(id+"F4.wireOp",EDGE,"E2.top")])]})}),makeQuery(id+"F7.opExtrude","SWEPT_FACE",FACE,{"disambiguationData":[OSD([sQuery(id+"F6.wireOp",EDGE,"E3")])]})]});
            var Q35;
            Q35=makeQuery(id+"F7.boolean.opBoolean","INTERSECT",EDGE,{"disambiguationData":[OD(1.0)],"derivedFrom":[makeQuery(id+"F5.boolean.opBoolean","COPY",FACE,{"derivedFrom":makeQuery(id+"F5.opExtrude","SWEPT_FACE",FACE,{"disambiguationData":[OSD([sQuery(id+"F4.wireOp",EDGE,"E2.bottom")])]})}),makeQuery(id+"F7.opExtrude","SWEPT_FACE",FACE,{"disambiguationData":[OSD([sQuery(id+"F6.wireOp",EDGE,"E3")])]})]});
            var Q36;
            Q36=makeQuery(id+"F7.boolean.opBoolean","INTERSECT",EDGE,{"disambiguationData":[OD(0.0)],"derivedFrom":[makeQuery(id+"F5.boolean.opBoolean","COPY",FACE,{"derivedFrom":makeQuery(id+"F5.opExtrude","SWEPT_FACE",FACE,{"disambiguationData":[OSD([sQuery(id+"F4.wireOp",EDGE,"E2.top")])]})}),makeQuery(id+"F7.opExtrude","SWEPT_FACE",FACE,{"disambiguationData":[OSD([sQuery(id+"F6.wireOp",EDGE,"E3")])]})]});
            var Q37;
            Q37=makeQuery(id+"F7.boolean.opBoolean","INTERSECT",EDGE,{"disambiguationData":[OD(0.0)],"derivedFrom":[makeQuery(id+"F5.boolean.opBoolean","COPY",FACE,{"derivedFrom":makeQuery(id+"F5.opExtrude","SWEPT_FACE",FACE,{"disambiguationData":[OSD([sQuery(id+"F4.wireOp",EDGE,"E2.bottom")])]})}),makeQuery(id+"F7.opExtrude","SWEPT_FACE",FACE,{"disambiguationData":[OSD([sQuery(id+"F6.wireOp",EDGE,"E3")])]})]});
            var Q38;
            Q38=makeQuery(id+"F5.boolean.opBoolean","INTERSECT",EDGE,{"disambiguationData":[OD(1.0)],"derivedFrom":[makeQuery(id+"F1.opExtrude","SWEPT_FACE",FACE,{"disambiguationData":[OSD([sQuery(id+"F0.wireOp",EDGE,"E0")])]}),makeQuery(id+"F5.opExtrude","SWEPT_FACE",FACE,{"disambiguationData":[OSD([sQuery(id+"F4.wireOp",EDGE,"E2.top")])]})]});
            var Q39;
            Q39=makeQuery(id+"F10.opFillet","BLEND_EDGE",EDGE,{"blendedFrom":[makeQuery(id+"F1.opExtrude","CAP_EDGE",EDGE,{"disambiguationData":[OSD([sQuery(id+"F0.wireOp",EDGE,"E0")])],"isStart":false}),makeQuery(id+"F7.boolean.opBoolean","SPLIT",FACE,{"disambiguationData":[OD(1.0)],"derivedFrom":makeQuery(id+"F5.boolean.opBoolean","COPY",FACE,{"derivedFrom":makeQuery(id+"F5.opExtrude","SWEPT_FACE",FACE,{"disambiguationData":[OSD([sQuery(id+"F4.wireOp",EDGE,"E2.bottom")])]})})})],"blendedInto":[makeQuery(id+"F7.boolean.opBoolean","SPLIT",FACE,{"disambiguationData":[OD(1.0)],"derivedFrom":makeQuery(id+"F5.boolean.opBoolean","COPY",FACE,{"derivedFrom":makeQuery(id+"F5.opExtrude","SWEPT_FACE",FACE,{"disambiguationData":[OSD([sQuery(id+"F4.wireOp",EDGE,"E2.bottom")])]})})})]});
            fillet(context, id + "F12", {"entities" : qUnion([Q0, Q1, Q2, Q3, Q4, Q5, Q6, Q7, Q8, Q9, Q10, Q11, Q12, Q13, Q14, Q15, Q16, Q17, Q18, Q19, Q20, Q21, Q22, Q23, Q24, Q25, Q26, Q27, Q28, Q29, Q30, Q31, Q32, Q33, Q34, Q35, Q36, Q37, Q38, Q39]), "radius" : .25 * mm, "tangentPropagation" : true, "allowEdgeOverflow" : false});
        }
    });
